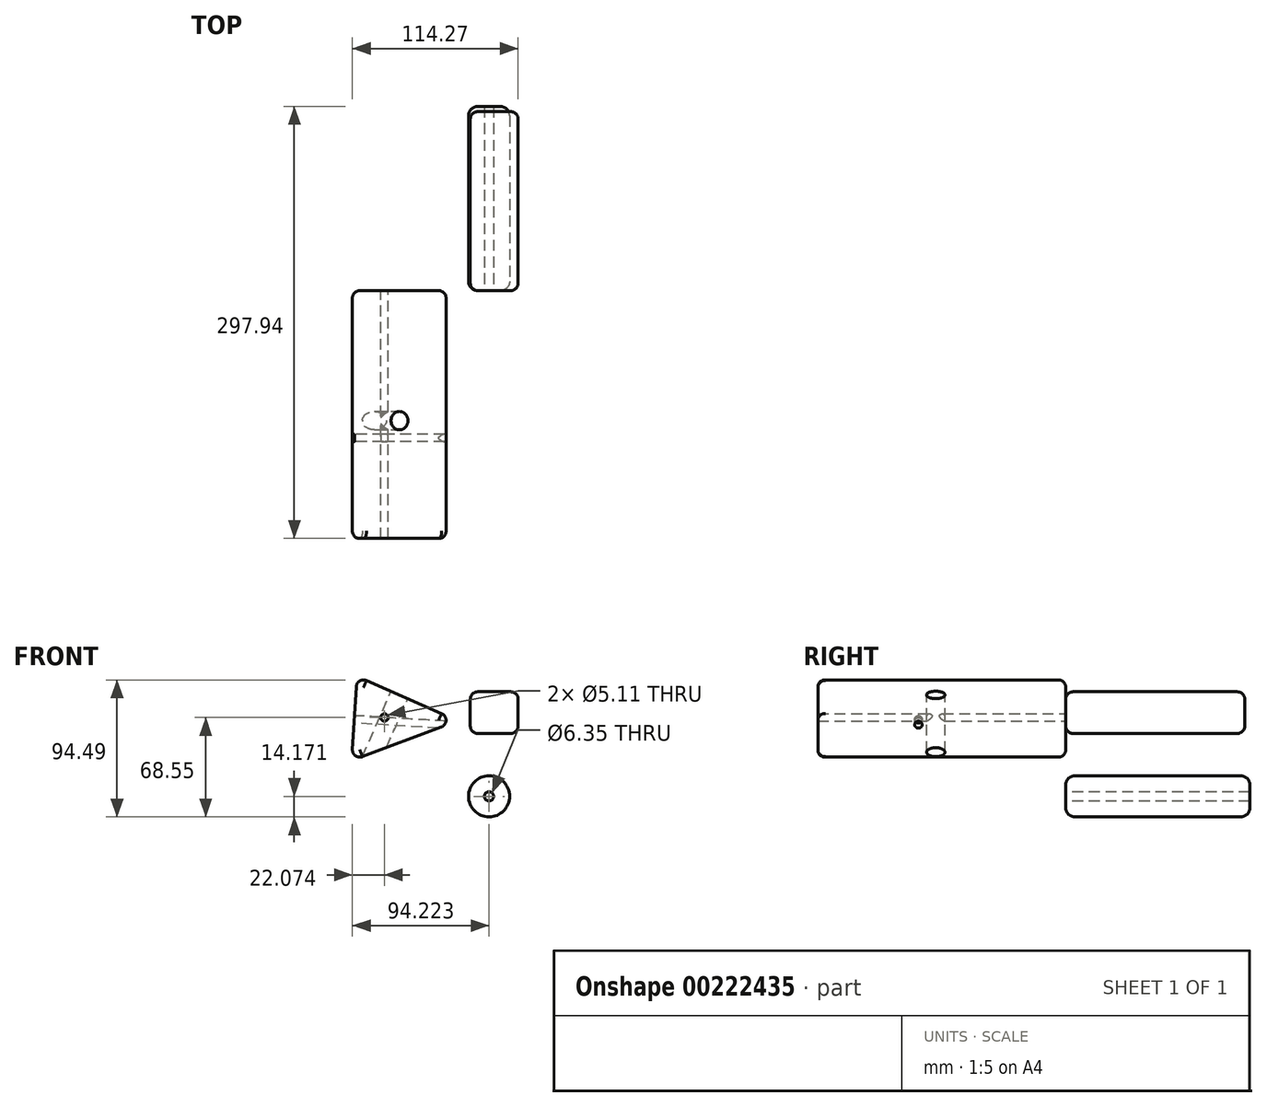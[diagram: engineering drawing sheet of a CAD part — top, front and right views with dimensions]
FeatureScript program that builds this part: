
annotation { "Feature Type Name" : "Feature", "Feature Type Description" : "" }
export const myFeature = defineFeature(function(context is Context, id is Id, definition is map)
    precondition{}
    {
        {
            var Q0;
            Q0=qCreatedBy(makeId("Front.planeOp"),FACE);
            var sketch = newSketch(context, id + "F0", { "sketchPlane" : qUnion([Q0])});
            skLineSegment(sketch, "E0", {"start": v(-54.35, 49.36) * mm, "end": v(15.61, 18.67) * mm});
            skLineSegment(sketch, "E1", {"start": v(15.61, 18.67) * mm, "end": v(-57.82, -8.89) * mm});
            skLineSegment(sketch, "E2", {"start": v(-57.82, -8.89) * mm, "end": v(-54.35, 49.36) * mm});
            skSolve(sketch);
        }
        {
            var Q0;
            Q0 = qSketchRegion(id + "F0", true);
            extrude(context, id + "F1", {"entities" : qUnion([Q0]), "depth" : 170.94 * mm});
        }
        {
            var Q0;
            Q0=makeQuery(id+"F1.opExtrude","CAP_EDGE",EDGE,{"disambiguationData":[OSD([sQuery(id+"F0.wireOp",EDGE,"E0")])],"isStart":false});
            fillet(context, id + "F2", {"entities" : qUnion([Q0]), "radius" : 5.08 * mm, "tangentPropagation" : true, "allowEdgeOverflow" : false});
        }
        {
            var Q0;
            Q0=makeQuery(id+"F1.opExtrude","SWEPT_EDGE",EDGE,{"disambiguationData":[OSD([sQuery(id+"F0.wireOp",EDGE,"E0"),sQuery(id+"F0.wireOp",EDGE,"E1")])]});
            var Q1;
            Q1=makeQuery(id+"F1.opExtrude","CAP_EDGE",EDGE,{"disambiguationData":[OSD([sQuery(id+"F0.wireOp",EDGE,"E2")])],"isStart":false});
            fillet(context, id + "F3", {"entities" : qUnion([Q0, Q1]), "radius" : 5.08 * mm, "tangentPropagation" : true, "allowEdgeOverflow" : false});
        }
        {
            var Q0;
            Q0=makeQuery(id+"F1.opExtrude","SWEPT_EDGE",EDGE,{"disambiguationData":[OSD([sQuery(id+"F0.wireOp",EDGE,"E1"),sQuery(id+"F0.wireOp",EDGE,"E2")])]});
            fillet(context, id + "F4", {"entities" : qUnion([Q0]), "radius" : 5.08 * mm, "tangentPropagation" : true, "allowEdgeOverflow" : false});
        }
        {
            var Q0;
            Q0=makeQuery(id+"F1.opExtrude","SWEPT_FACE",FACE,{"disambiguationData":[OSD([sQuery(id+"F0.wireOp",EDGE,"E2")])]});
            fillet(context, id + "F5", {"entities" : qUnion([Q0]), "radius" : 5.08 * mm, "tangentPropagation" : true, "allowEdgeOverflow" : false});
        }
        {
            var Q0;
            Q0=makeQuery(id+"F1.opExtrude","SWEPT_FACE",FACE,{"disambiguationData":[OSD([sQuery(id+"F0.wireOp",EDGE,"E2")])]});
            var sketch = newSketch(context, id + "F6", { "sketchPlane" : qUnion([Q0])});
            skCircle(sketch, "E3", {"center": v(101.6, 16.27) * mm, "radius": 7.13 * mm});
            skSolve(sketch);
        }
        {
            var Q0;
            Q0=sQuery(id+"F6.wireOp",VERTEX,"E3.center");
            var Q1;
            Q1=makeQuery(id+"F1.opExtrude","SWEPT_BODY",BODY,{"disambiguationData":[OSD([sQuery(id+"F0.wireOp",EDGE,"E0"),sQuery(id+"F0.wireOp",EDGE,"E1"),sQuery(id+"F0.wireOp",EDGE,"E2")])]});
            hole(context, id + "F7", {"style" : HoleStyle.SIMPLE, "endStyle" : HoleEndStyle.THROUGH, "standardTappedOrClearance" : lookupTablePath({ "standard" : "ANSI", "engagement" : "75%", "pitch" : "20 tpi", "size" : "1/4", "type" : "Tapped" }), "standardBlindInLast" : lookupTablePath({ "standard" : "ANSI", "engagement" : "75%", "pitch" : "20 tpi", "size" : "1/4", "type" : "Tapped" }), "holeDiameter" : 5.1 * mm, "locations" : qUnion([Q0]), "scope" : qUnion([Q1]), "isTappedThrough" : true, "majorDiameter" : 6.35 * mm, "showTappedDepth" : true});
        }
        {
            var Q0;
            Q0=qCreatedBy(makeId("Front.planeOp"),FACE);
            var sketch = newSketch(context, id + "F8", { "sketchPlane" : qUnion([Q0])});
            skLineSegment(sketch, "E4.bottom", {"start": v(23.92, 38.63) * mm, "end": v(56.9, 38.63) * mm});
            skLineSegment(sketch, "E4.top", {"start": v(23.92, 9.86) * mm, "end": v(56.9, 9.86) * mm});
            skLineSegment(sketch, "E4.left", {"start": v(23.92, 38.63) * mm, "end": v(23.92, 9.86) * mm});
            skLineSegment(sketch, "E4.right", {"start": v(56.9, 38.63) * mm, "end": v(56.9, 9.86) * mm});
            skSolve(sketch);
        }
        {
            var Q0;
            Q0=makeQuery(id+"F8.imprint","IMPRINT",FACE,{"disambiguationData":[TD([[makeQuery(id+"F8.imprint","IMPRINT",EDGE,{"derivedFrom":sQuery(id+"F8.wireOp",EDGE,"E4.bottom")}),-1.0]])]});
            extrude(context, id + "F9", {"entities" : qUnion([Q0]), "oppositeDirection" : true, "depth" : 123.44 * mm});
        }
        {
            var Q0;
            Q0=makeQuery(id+"F9.opExtrude","SWEPT_EDGE",EDGE,{"disambiguationData":[OSD([sQuery(id+"F8.wireOp",EDGE,"E4.top"),sQuery(id+"F8.wireOp",EDGE,"E4.left")])]});
            var Q1;
            Q1=makeQuery(id+"F9.opExtrude","SWEPT_EDGE",EDGE,{"disambiguationData":[OSD([sQuery(id+"F8.wireOp",EDGE,"E4.top"),sQuery(id+"F8.wireOp",EDGE,"E4.right")])]});
            var Q2;
            Q2=makeQuery(id+"F9.opExtrude","CAP_EDGE",EDGE,{"disambiguationData":[OSD([sQuery(id+"F8.wireOp",EDGE,"E4.top")])],"isStart":false});
            var Q3;
            Q3=makeQuery(id+"F9.opExtrude","CAP_EDGE",EDGE,{"disambiguationData":[OSD([sQuery(id+"F8.wireOp",EDGE,"E4.right")])],"isStart":false});
            var Q4;
            Q4=makeQuery(id+"F9.opExtrude","CAP_EDGE",EDGE,{"disambiguationData":[OSD([sQuery(id+"F8.wireOp",EDGE,"E4.bottom")])],"isStart":false});
            var Q5;
            Q5=makeQuery(id+"F9.opExtrude","CAP_EDGE",EDGE,{"disambiguationData":[OSD([sQuery(id+"F8.wireOp",EDGE,"E4.left")])],"isStart":false});
            var Q6;
            Q6=makeQuery(id+"F9.opExtrude","SWEPT_EDGE",EDGE,{"disambiguationData":[OSD([sQuery(id+"F8.wireOp",EDGE,"E4.bottom"),sQuery(id+"F8.wireOp",EDGE,"E4.right")])]});
            var Q7;
            Q7=makeQuery(id+"F9.opExtrude","SWEPT_EDGE",EDGE,{"disambiguationData":[OSD([sQuery(id+"F8.wireOp",EDGE,"E4.bottom"),sQuery(id+"F8.wireOp",EDGE,"E4.left")])]});
            var Q8;
            Q8=makeQuery(id+"F9.opExtrude","CAP_EDGE",EDGE,{"disambiguationData":[OSD([sQuery(id+"F8.wireOp",EDGE,"E4.bottom")])],"isStart":true});
            var Q9;
            Q9=makeQuery(id+"F9.opExtrude","CAP_EDGE",EDGE,{"disambiguationData":[OSD([sQuery(id+"F8.wireOp",EDGE,"E4.top")])],"isStart":true});
            var Q10;
            Q10=makeQuery(id+"F9.opExtrude","CAP_EDGE",EDGE,{"disambiguationData":[OSD([sQuery(id+"F8.wireOp",EDGE,"E4.right")])],"isStart":true});
            var Q11;
            Q11=makeQuery(id+"F9.opExtrude","CAP_EDGE",EDGE,{"disambiguationData":[OSD([sQuery(id+"F8.wireOp",EDGE,"E4.left")])],"isStart":true});
            fillet(context, id + "F10", {"entities" : qUnion([Q0, Q1, Q2, Q3, Q4, Q5, Q6, Q7, Q8, Q9, Q10, Q11]), "radius" : 5.08 * mm, "tangentPropagation" : true, "allowEdgeOverflow" : false});
        }
        {
            var Q0;
            Q0=makeQuery(id+"F1.opExtrude","SWEPT_FACE",FACE,{"disambiguationData":[OSD([sQuery(id+"F0.wireOp",EDGE,"E0")])]});
            var sketch = newSketch(context, id + "F11", { "sketchPlane" : qUnion([Q0])});
            skCircle(sketch, "E5", {"center": v(-37.45, -89.66) * mm, "radius": 9.53 * mm});
            skSolve(sketch);
        }
        {
            var Q0;
            Q0=sQuery(id+"F11.wireOp",VERTEX,"E5.center");
            var Q1;
            Q1=makeQuery(id+"F1.opExtrude","SWEPT_BODY",BODY,{"disambiguationData":[OSD([sQuery(id+"F0.wireOp",EDGE,"E0"),sQuery(id+"F0.wireOp",EDGE,"E1"),sQuery(id+"F0.wireOp",EDGE,"E2")])]});
            hole(context, id + "F12", {"style" : HoleStyle.SIMPLE, "endStyle" : HoleEndStyle.THROUGH, "holeDiameter" : 12.7 * mm, "locations" : qUnion([Q0]), "scope" : qUnion([Q1]), "isTappedThrough" : true});
        }
        {
            var Q0;
            Q0=qCreatedBy(makeId("Front.planeOp"),FACE);
            var sketch = newSketch(context, id + "F13", { "sketchPlane" : qUnion([Q0])});
            skCircle(sketch, "E6", {"center": v(36.85, -33.46) * mm, "radius": 14.17 * mm});
            skSolve(sketch);
        }
        {
            var Q0;
            Q0 = qSketchRegion(id + "F13", true);
            extrude(context, id + "F14", {"entities" : qUnion([Q0]), "oppositeDirection" : true, "depth" : 127 * mm});
        }
        {
            var Q0;
            Q0=makeQuery(id+"F14.opExtrude","CAP_EDGE",EDGE,{"disambiguationData":[OSD([sQuery(id+"F13.wireOp",EDGE,"E6")])],"isStart":true});
            var Q1;
            Q1=makeQuery(id+"F14.opExtrude","CAP_EDGE",EDGE,{"disambiguationData":[OSD([sQuery(id+"F13.wireOp",EDGE,"E6")])],"isStart":false});
            fillet(context, id + "F15", {"entities" : qUnion([Q0, Q1]), "radius" : 6.35 * mm, "tangentPropagation" : true, "allowEdgeOverflow" : false});
        }
        {
            var Q0;
            Q0=makeQuery(id+"F14.opExtrude","CAP_FACE",FACE,{"disambiguationData":[OSD([sQuery(id+"F13.wireOp",EDGE,"E6")])],"isStart":true});
            var sketch = newSketch(context, id + "F16", { "sketchPlane" : qUnion([Q0])});
            skCircle(sketch, "E7", {"center": v(36.85, -33.46) * mm, "radius": 3.18 * mm});
            skSolve(sketch);
        }
        {
            var Q0;
            Q0=sQuery(id+"F16.wireOp",VERTEX,"E7.center");
            var Q1;
            Q1=makeQuery(id+"F14.opExtrude","SWEPT_BODY",BODY,{"disambiguationData":[OSD([sQuery(id+"F13.wireOp",EDGE,"E6")])]});
            hole(context, id + "F17", {"style" : HoleStyle.SIMPLE, "endStyle" : HoleEndStyle.THROUGH, "holeDiameter" : 6.35 * mm, "locations" : qUnion([Q0]), "scope" : qUnion([Q1]), "isTappedThrough" : true});
        }
        {
            var Q0;
            Q0=makeQuery(id+"F1.opExtrude","CAP_FACE",FACE,{"disambiguationData":[OSD([sQuery(id+"F0.wireOp",EDGE,"E0"),sQuery(id+"F0.wireOp",EDGE,"E1"),sQuery(id+"F0.wireOp",EDGE,"E2")])],"isStart":true});
            var sketch = newSketch(context, id + "F18", { "sketchPlane" : qUnion([Q0])});
            skPoint(sketch, "E8", {"position": v(35.3, 20.92) * mm});
            skSolve(sketch);
        }
        {
            var Q0;
            Q0=sQuery(id+"F18.wireOp",VERTEX,"E8");
            var Q1;
            Q1=makeQuery(id+"F1.opExtrude","SWEPT_BODY",BODY,{"disambiguationData":[OSD([sQuery(id+"F0.wireOp",EDGE,"E0"),sQuery(id+"F0.wireOp",EDGE,"E1"),sQuery(id+"F0.wireOp",EDGE,"E2")])]});
            hole(context, id + "F19", {"style" : HoleStyle.SIMPLE, "endStyle" : HoleEndStyle.THROUGH, "standardTappedOrClearance" : lookupTablePath({ "standard" : "ANSI", "engagement" : "75%", "pitch" : "20 tpi", "size" : "1/4", "type" : "Tapped" }), "standardBlindInLast" : lookupTablePath({ "standard" : "ANSI", "engagement" : "75%", "pitch" : "20 tpi", "size" : "1/4", "type" : "Tapped" }), "holeDiameter" : 5.1 * mm, "locations" : qUnion([Q0]), "scope" : qUnion([Q1]), "isTappedThrough" : true, "majorDiameter" : 6.35 * mm, "showTappedDepth" : true});
        }
    });
